# Revit family: Haworth_Enclose_Wall_GlassTransom
name_source: partatom
category: Furniture Systems
revit_build: Autodesk Revit 2018 (Build: 20170223_1515(x64)
units: mm (PartAtom-declared; Revit-internal decimal feet)

## family parameters
Always vertical = Yes
Cut with Voids When Loaded = No
OmniClass Number = 23.25.40.14
OmniClass Title = Demountable Partitions
Part Type = Normal
Room Calculation Point = No
Round Connector Dimension = Use Diameter
Shared = Yes
Work Plane-Based = No

## types (7) — shared parameters
# of Muntins = 2
AFF Muntin 1 = 30 "
AFF Muntin 2 = 60 "
Actual # of Muntins = 2
Actual AFF Muntin 1 = 30 "
Actual AFF Muntin 2 = 60 "
Actual Glass Panel Height = 88 "
Actual Height = 108 "
Assembly Code = C1010200
Base Height = 1.25 "
Cap Height = 1 "
Ceiling Mount = Yes
Description = Wall Glass Transom
End of Run Finish = Haworth _ Polymer _ Black
End of Run Width = 0.155 "
Frame Depth = 4 "
Frame Finish = Haworth _ Metal _ Brushed Aluminum
Glass Finish = Haworth _ Glass _ Clear
Glass Offset = 4.745 "
Glass Panel Height = 88 "
Height = 108 "
Horizontal Bottom Adjuster Width = 3.87 "
Horizontal Bottom Trim Width = 2.425 "
Horizontal Frame Width = 0.875 "
Horizontal Top Adjuster Width = 2.625 "
Horizontal Top Trim Width = 1.43 "
Horizontal Transom Frame Width = 2.5 "
Manufacturer = Haworth
Material Options = http://surfaces.haworth.com
Max # of Muntins = 2
Max. Height = 144 "
Max. Width = 60 "
Min. Height = 92 "
Min. Spacing Between Muntins = 8 "
Min. Width = 8 "
Min/Max Height = 92-144 in.
Min/Max Width = 8-60 in.
Model = Haworth - Enclose
Muntin Note = Bottom Muntin is Muntin 1
Muntin Width = 0.875 "
Panel Depth = 0.4 "
Panel Height 1 = 83.255 "
Panel Height 2 = 14 "
Revision Number = 3
Size = Verify Final Dim. w/ Haworth
Sustainability Info = http://www.haworth.com
Too Many Muntins = No
Transom Panel Height = 20 "
URL = www.haworth.com
URL - Product = http://www.haworth.com
Vertical Frame Width = 0.875 "
Warranty = http://www.haworth.com

## per-type parameters (varying)
| type | Actual Width | Panel Width | Width |
| 36" x 108" | 36 " | 33.94 " | 36 " |
| 24" x 108" | 24 " | 21.94 " | 24 " |
| 30" x 108" | 30 " | 27.94 " | 30 " |
| 42" x 108" | 42 " | 39.94 " | 42 " |
| 48" x 108" | 48 " | 45.94 " | 48 " |
| 54" x 108" | 54 " | 51.94 " | 54 " |
| 60" x 108" | 60 " | 57.94 " | 60 " |

## geometry (parser evidence)
native form markers: Sweep x10
no freeform markers — native parametric forms only
